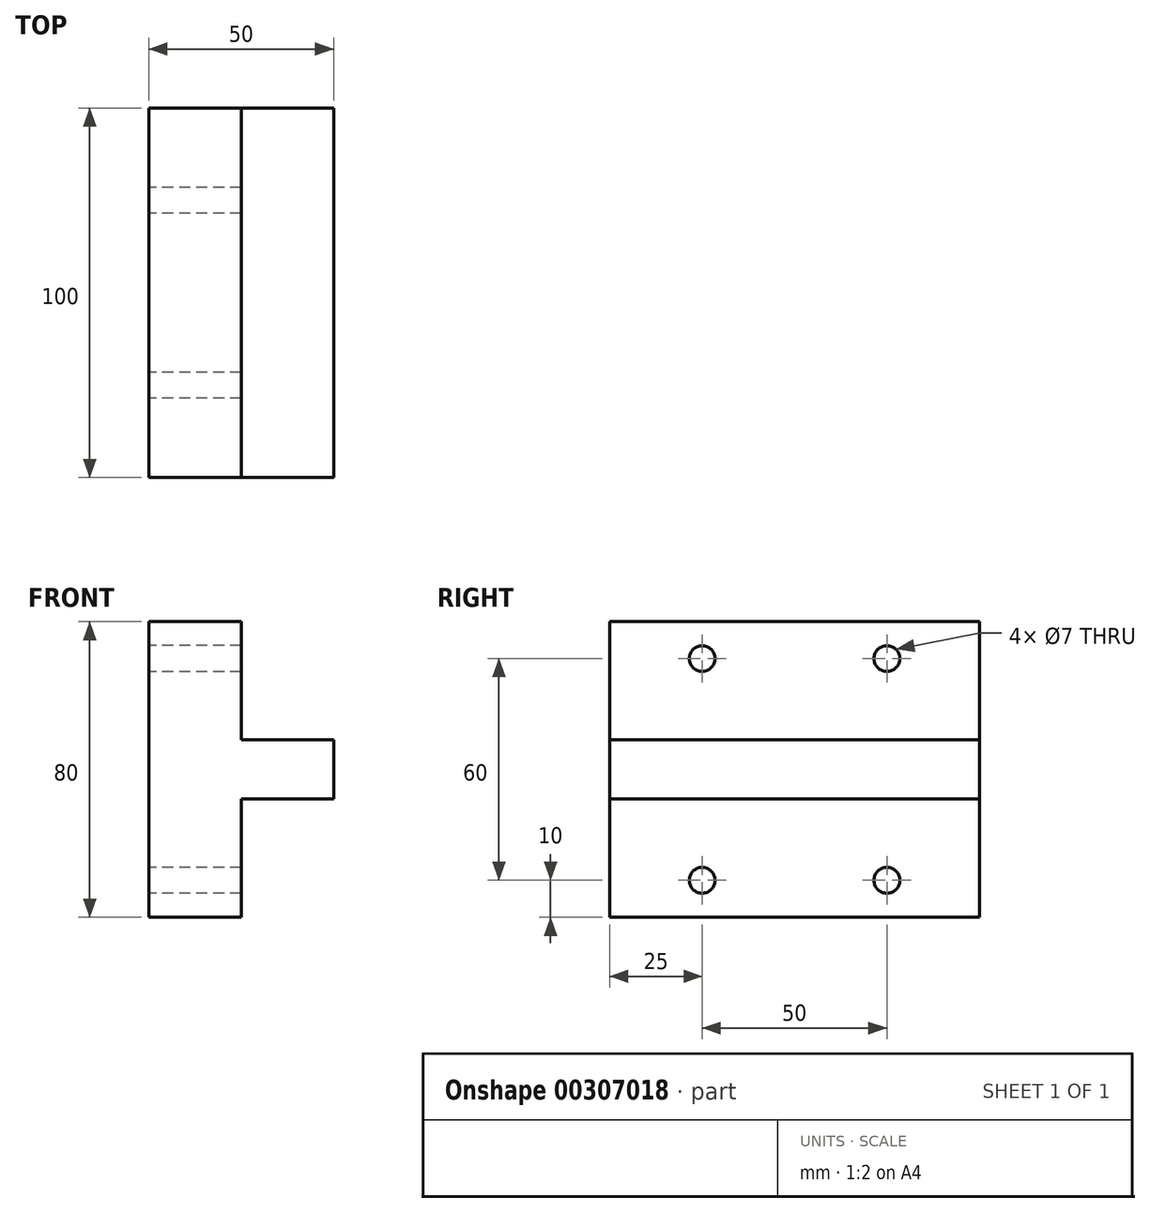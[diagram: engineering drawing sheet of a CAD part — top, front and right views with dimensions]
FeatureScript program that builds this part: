
annotation { "Feature Type Name" : "Feature", "Feature Type Description" : "" }
export const myFeature = defineFeature(function(context is Context, id is Id, definition is map)
    precondition{}
    {
        {
            var Q0;
            Q0=qCreatedBy(makeId("Front.planeOp"),FACE);
            var sketch = newSketch(context, id + "F0", { "sketchPlane" : qUnion([Q0])});
            skLineSegment(sketch, "E0.left", {"start": v(5.19, 0) * mm, "end": v(5.19, -40) * mm});
            skLineSegment(sketch, "E0.right", {"start": v(55.19, 8) * mm, "end": v(55.19, -8) * mm});
            skLineSegment(sketch, "E1", {"start": v(5.19, 0) * mm, "end": v(5.19, 0) * mm});
            skLineSegment(sketch, "E2", {"start": v(5.19, 0) * mm, "end": v(5.19, 40) * mm});
            skLineSegment(sketch, "E3", {"start": v(55.19, 8) * mm, "end": v(30.19, 8) * mm});
            skLineSegment(sketch, "E4", {"start": v(30.19, 8) * mm, "end": v(30.19, 40) * mm});
            skLineSegment(sketch, "E5", {"start": v(30.19, 40) * mm, "end": v(5.19, 40) * mm});
            skLineSegment(sketch, "E6", {"start": v(5.19, -40) * mm, "end": v(30.19, -40) * mm});
            skLineSegment(sketch, "E7", {"start": v(30.19, -40) * mm, "end": v(30.19, -8) * mm});
            skLineSegment(sketch, "E8", {"start": v(30.19, -8) * mm, "end": v(55.19, -8) * mm});
            skSolve(sketch);
        }
        {
            var Q0;
            Q0=qSketchRegion(id+"F0",true);
            extrude(context, id + "F1", {"entities" : qUnion([Q0]), "depth" : 100 * mm});
        }
        {
            var Q0;
            Q0=makeQuery(id+"F1.opExtrude","SWEPT_FACE",FACE,{"disambiguationData":[OSD([sQuery(id+"F0.wireOp",EDGE,"E2")])]});
            var sketch = newSketch(context, id + "F2", { "sketchPlane" : qUnion([Q0])});
            skCircle(sketch, "E9", {"center": v(25, 30) * mm, "radius": 3.5 * mm});
            skCircle(sketch, "E10", {"center": v(75, 30) * mm, "radius": 3.5 * mm});
            skCircle(sketch, "E11", {"center": v(25, -30) * mm, "radius": 3.5 * mm});
            skCircle(sketch, "E12", {"center": v(75, -30) * mm, "radius": 3.5 * mm});
            skSolve(sketch);
        }
        {
            var Q0;
            Q0=qSketchRegion(id+"F2",true);
            extrude(context, id + "F3", {"entities" : qUnion([Q0]), "operationType" : NewBodyOperationType.REMOVE, "oppositeDirection" : true, "depth" : 100 * mm, "symmetric" : true});
        }
    });
